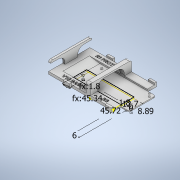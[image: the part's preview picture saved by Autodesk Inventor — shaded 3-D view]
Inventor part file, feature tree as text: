
AUTODESK INVENTOR PART (.ipt)
format: ipt  version: 2021 (Build 250183000, 183)  size: 1,721,344 bytes
history: native  units: in
note: dims shown in document units (in); Inventor stores cm internally (conversion verified against a paired STEP export)
features: sketch x13, extrude x12, fillet x5, mirror x3, plane x2, chamfer x1
ambient origin geometry x8: Origin, YZ Plane, XZ Plane, XY Plane, X Axis, Y Axis, Z Axis, Center Point
bodies: Solid1 (feature_tree)
feature tree (36):
  extrude  "Extrusion1"  Depth=0.7756in
  extrude  "Extrusion2"  Depth=0.2362in
  plane  "Work Plane1"
  extrude  "Extrusion3"  Depth=0.2362in
  sketch  "Sketch5"  dims[d14=1.3386in d15=0.0in]
  extrude  "Extrusion4"  TaperAngle=0.0deg  [1 undecoded]
  sketch  "Sketch7"  dims[d19=0.8661in d20=0.378in d21=0.0in d22=0.7756in]
  extrude  "Extrusion5"  Depth=0.1575in
  plane  "Work Plane2"
  extrude  "Extrusion8"  Depth=0.378in
  fillet  "Fillet3"  [1 undecoded]
  fillet  "Fillet4"  Radius=0.7756in
  sketch  "Sketch13"  dims[d26=1.4803in]
  extrude  "Extrusion9"  Depth=0.5in
  mirror  "Mirror3"
  chamfer  "Chamfer1"  Distance=0.748in
  extrude  "Extrusion11"  Depth=0.5in
  extrude  "Extrusion12"  Depth=0.0787in
  extrude  "Extrusion13"  Depth=0.0709in
  mirror  "Mirror4"
  fillet  "Fillet5"  Radius=0.0709in
  extrude  "Extrusion14"  Depth=1.8in
  extrude  "Extrusion15"  Depth=0.35in
  mirror  "Mirror5"
  fillet  "Fillet8"  Radius=0.1181in
  fillet  "Fillet9"  Radius=0.3937in
  sketch  "Sketch1"  dims[d5=2.4409in d6=0.7756in]
  sketch  "Sketch3"  dims[d7=0.0945in d8=0.0in d9=0.2362in]
  sketch  "Sketch4"  dims[d10=0.0787in d11=0.0in d13=0.2362in]
  sketch  "Sketch6"  dims[d16=0.063in d17=0.0in d18=0.1575in]
  sketch  "Sketch8"  dims[d23=0.378in d24=0.5in]
  sketch  "Sketch12"  dims[d25=0.3189in]
  sketch  "Sketch15"  dims[d27=0.0in d29=-0.748in d30=0.748in]
  sketch  "Sketch16"  dims[d41=1.785in d42=0.5in]
  sketch  "Sketch18"  dims[d43=0.0551in d44=0.0in d46=0.0787in]
  sketch  "Sketch19"  dims[d47=0.2756in d48=0.0709in d49=0.0709in d50=1.8in d51=0.35in d52=0.1181in d53=0.0in d56=0.3937in d57=0.0551in d58=45.0deg d59=0.0787in d60=0.0787in d61=0.0394in d62=0.0394in d63=0.0394in d64=0.0394in d65=0.0787in d66=0.0787in d67=0.0394in d68=0.0in d69=0.0in d70=0.0in d71=0.2397in d72=0.2397in d73=1.0in d74=0.315in d75=0.0in d76=0.2362in d77=0.0394in d78=0.0in d79=0.0945in d80=0.0787in d84=0.2992in d85=0.0in d86=0.0in d87=0.0787in d90=0.0787in d91=0.7756in d92=0.0787in d93=0.0in d96=0.0in d97=0.2362in d98=0.2756in d99=0.0787in d100=0.0in]
note: 2 required parameter values undecoded (feature->parameter linkage not recoverable at this tier; creation-order binding heuristic only, values carry confidence <= 0.55)
